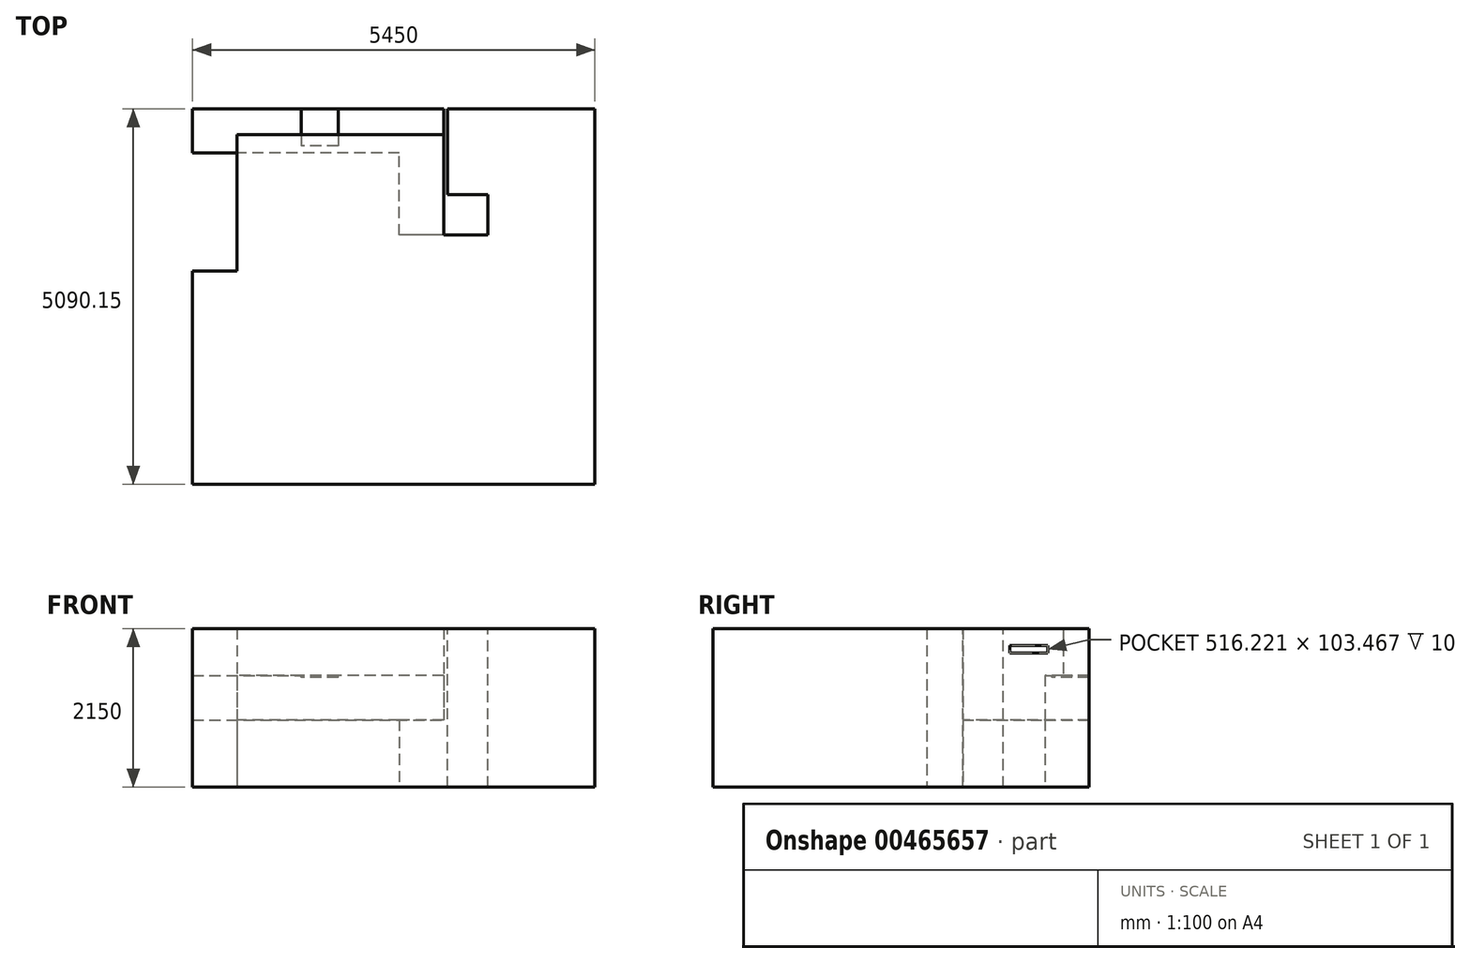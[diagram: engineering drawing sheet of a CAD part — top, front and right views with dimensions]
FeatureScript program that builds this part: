
annotation { "Feature Type Name" : "Feature", "Feature Type Description" : "" }
export const myFeature = defineFeature(function(context is Context, id is Id, definition is map)
    precondition{}
    {
        {
            var Q0;
            Q0=qCreatedBy(makeId("Top.planeOp"),FACE);
            var sketch = newSketch(context, id + "F0", { "sketchPlane" : qUnion([Q0])});
            skLineSegment(sketch, "E0", {"start": v(-1473.18, -1123.99) * mm, "end": v(-1473.18, 1076.01) * mm});
            skLineSegment(sketch, "E1", {"start": v(-1473.18, 1076.01) * mm, "end": v(1926.82, 1076.01) * mm});
            skLineSegment(sketch, "E2", {"start": v(1926.82, 1076.01) * mm, "end": v(1926.82, -633.99) * mm});
            skLineSegment(sketch, "E3", {"start": v(1926.82, -633.99) * mm, "end": v(1326.82, -633.99) * mm});
            skLineSegment(sketch, "E4", {"start": v(1326.82, -633.99) * mm, "end": v(1326.82, 476.01) * mm});
            skLineSegment(sketch, "E5", {"start": v(1326.82, 476.01) * mm, "end": v(-873.18, 476.01) * mm});
            skLineSegment(sketch, "E6", {"start": v(-873.18, 476.01) * mm, "end": v(-873.18, -1123.99) * mm});
            skLineSegment(sketch, "E7", {"start": v(-873.18, -1123.99) * mm, "end": v(-1473.18, -1123.99) * mm});
            skSolve(sketch);
        }
        {
            var Q0;
            Q0=makeQuery(id+"F0.imprint","IMPRINT",FACE,{"disambiguationData":[TD([[makeQuery(id+"F0.imprint","IMPRINT",EDGE,{"derivedFrom":sQuery(id+"F0.wireOp",EDGE,"E0")}),-1.0]])]});
            extrude(context, id + "F1", {"entities" : qUnion([Q0]), "depth" : 910 * mm});
        }
        {
            var Q0;
            Q0=makeQuery(id+"F1.opExtrude","CAP_FACE",FACE,{"disambiguationData":[OSD([sQuery(id+"F0.wireOp",EDGE,"E0"),sQuery(id+"F0.wireOp",EDGE,"E1"),sQuery(id+"F0.wireOp",EDGE,"E2"),sQuery(id+"F0.wireOp",EDGE,"E3"),sQuery(id+"F0.wireOp",EDGE,"E4"),sQuery(id+"F0.wireOp",EDGE,"E5"),sQuery(id+"F0.wireOp",EDGE,"E6"),sQuery(id+"F0.wireOp",EDGE,"E7")])],"isStart":false});
            var sketch = newSketch(context, id + "F2", { "sketchPlane" : qUnion([Q0])});
            skLineSegment(sketch, "E8.bottom", {"start": v(-1473.18, -1123.99) * mm, "end": v(-873.18, -1123.99) * mm});
            skLineSegment(sketch, "E8.top", {"start": v(-1473.18, 476.01) * mm, "end": v(-873.18, 476.01) * mm});
            skLineSegment(sketch, "E8.left", {"start": v(-1473.18, -1123.99) * mm, "end": v(-1473.18, 476.01) * mm});
            skLineSegment(sketch, "E8.right", {"start": v(-873.18, -1123.99) * mm, "end": v(-873.18, 476.01) * mm});
            skSolve(sketch);
        }
        {
            var Q0;
            Q0=makeQuery(id+"F2.imprint","IMPRINT",FACE,{"disambiguationData":[TD([[makeQuery(id+"F2.imprint","IMPRINT",EDGE,{"derivedFrom":sQuery(id+"F2.wireOp",EDGE,"E8.bottom")}),-1.0]])]});
            extrude(context, id + "F3", {"entities" : qUnion([Q0]), "operationType" : NewBodyOperationType.ADD, "depth" : 605 * mm});
        }
        {
            var Q0;
            Q0=makeQuery(id+"F3.opExtrude","CAP_FACE",FACE,{"disambiguationData":[OSD([sQuery(id+"F2.wireOp",EDGE,"E8.bottom"),sQuery(id+"F2.wireOp",EDGE,"E8.top"),sQuery(id+"F2.wireOp",EDGE,"E8.left"),sQuery(id+"F2.wireOp",EDGE,"E8.right")])],"isStart":false});
            var sketch = newSketch(context, id + "F4", { "sketchPlane" : qUnion([Q0])});
            skLineSegment(sketch, "E9", {"start": v(-873.18, -1123.99) * mm, "end": v(-1473.18, -1123.99) * mm});
            skLineSegment(sketch, "E10", {"start": v(-1473.18, -1123.99) * mm, "end": v(-1473.18, 1076.01) * mm});
            skLineSegment(sketch, "E11", {"start": v(-1473.18, 1076.01) * mm, "end": v(1926.82, 1076.01) * mm});
            skLineSegment(sketch, "E12", {"start": v(1926.82, 1076.01) * mm, "end": v(1926.82, 726.01) * mm});
            skLineSegment(sketch, "E13", {"start": v(1926.82, 726.01) * mm, "end": v(-873.18, 726.01) * mm});
            skLineSegment(sketch, "E14", {"start": v(-873.18, 726.01) * mm, "end": v(-873.18, 476.01) * mm});
            skLineSegment(sketch, "E15", {"start": v(-873.18, 476.01) * mm, "end": v(-873.18, 476.01) * mm});
            skLineSegment(sketch, "E16", {"start": v(-873.18, 476.01) * mm, "end": v(-873.18, -1123.99) * mm});
            skSolve(sketch);
        }
        {
            var Q0;
            {var subQ0=sQuery(id+"F4.wireOp",EDGE,"E11");Q0=makeQuery(id+"F4.imprint","IMPRINT",FACE,{"disambiguationData":[TD([[makeQuery(id+"F4.imprint","IMPRINT",EDGE,{"derivedFrom":subQ0}),-1.0]])]});}
            var Q1;
            {var subQ0=sQuery(id+"F4.wireOp",EDGE,"E9");Q1=makeQuery(id+"F4.imprint","IMPRINT",FACE,{"disambiguationData":[TD([[makeQuery(id+"F4.imprint","IMPRINT",EDGE,{"derivedFrom":subQ0}),-1.0]])]});}
            extrude(context, id + "F5", {"entities" : qUnion([Q0, Q1]), "operationType" : NewBodyOperationType.ADD, "depth" : 635 * mm});
        }
        {
            var Q0;
            Q0=makeQuery(id+"F5.opExtrude","CAP_FACE",FACE,{"disambiguationData":[OSD([sQuery(id+"F4.wireOp",EDGE,"E9"),sQuery(id+"F4.wireOp",EDGE,"E10"),sQuery(id+"F4.wireOp",EDGE,"E11"),sQuery(id+"F4.wireOp",EDGE,"E12"),sQuery(id+"F4.wireOp",EDGE,"E13"),sQuery(id+"F4.wireOp",EDGE,"E14"),sQuery(id+"F4.wireOp",EDGE,"E16")])],"isStart":true});
            var sketch = newSketch(context, id + "F6", { "sketchPlane" : qUnion([Q0])});
            skLineSegment(sketch, "E17.left", {"start": v(500, -1076.01) * mm, "end": v(500, -576.01) * mm});
            skLineSegment(sketch, "E17.right", {"start": v(0, -1076.01) * mm, "end": v(0, -576.01) * mm});
            skLineSegment(sketch, "E18", {"start": v(500, -1076.01) * mm, "end": v(0, -1076.01) * mm});
            skLineSegment(sketch, "E19", {"start": v(500, -576.01) * mm, "end": v(0, -576.01) * mm});
            skSolve(sketch);
        }
        {
            var Q0;
            {var subQ0=sQuery(id+"F6.wireOp",EDGE,"E19");Q0=makeQuery(id+"F6.imprint","IMPRINT",FACE,{"disambiguationData":[TD([[makeQuery(id+"F6.imprint","IMPRINT",EDGE,{"derivedFrom":subQ0}),1.0]])]});}
            var Q1;
            {var subQ0=sQuery(id+"F6.wireOp",EDGE,"E18");Q1=makeQuery(id+"F6.imprint","IMPRINT",FACE,{"disambiguationData":[TD([[makeQuery(id+"F6.imprint","IMPRINT",EDGE,{"derivedFrom":subQ0}),1.0]])]});}
            extrude(context, id + "F7", {"entities" : qUnion([Q0, Q1]), "operationType" : NewBodyOperationType.ADD, "depth" : 25 * mm});
        }
        {
            var Q0;
            Q0=makeQuery(id+"F1.opExtrude","CAP_FACE",FACE,{"disambiguationData":[OSD([sQuery(id+"F0.wireOp",EDGE,"E0"),sQuery(id+"F0.wireOp",EDGE,"E1"),sQuery(id+"F0.wireOp",EDGE,"E2"),sQuery(id+"F0.wireOp",EDGE,"E3"),sQuery(id+"F0.wireOp",EDGE,"E4"),sQuery(id+"F0.wireOp",EDGE,"E5"),sQuery(id+"F0.wireOp",EDGE,"E6"),sQuery(id+"F0.wireOp",EDGE,"E7")])],"isStart":true});
            var sketch = newSketch(context, id + "F8", { "sketchPlane" : qUnion([Q0])});
            skLineSegment(sketch, "E20.bottom", {"start": v(1926.82, -1076.01) * mm, "end": v(1976.82, -1076.01) * mm});
            skLineSegment(sketch, "E20.top", {"start": v(1926.82, 633.99) * mm, "end": v(1976.82, 633.99) * mm});
            skLineSegment(sketch, "E20.left", {"start": v(1926.82, -1076.01) * mm, "end": v(1926.82, 633.99) * mm});
            skLineSegment(sketch, "E20.right", {"start": v(1976.82, -1076.01) * mm, "end": v(1976.82, 633.99) * mm});
            skSolve(sketch);
        }
        {
            var Q0;
            Q0=makeQuery(id+"F8.imprint","IMPRINT",FACE,{"disambiguationData":[TD([[makeQuery(id+"F8.imprint","IMPRINT",EDGE,{"derivedFrom":sQuery(id+"F8.wireOp",EDGE,"E20.bottom")}),1.0]])]});
            var Q1;
            Q1=makeQuery(id+"F5.opExtrude","CAP_FACE",FACE,{"disambiguationData":[OSD([sQuery(id+"F4.wireOp",EDGE,"E9"),sQuery(id+"F4.wireOp",EDGE,"E10"),sQuery(id+"F4.wireOp",EDGE,"E11"),sQuery(id+"F4.wireOp",EDGE,"E12"),sQuery(id+"F4.wireOp",EDGE,"E13"),sQuery(id+"F4.wireOp",EDGE,"E14"),sQuery(id+"F4.wireOp",EDGE,"E16")])],"isStart":false});
            extrude(context, id + "F9", {"entities" : qUnion([Q0]), "operationType" : NewBodyOperationType.ADD, "endBound" : BoundingType.UP_TO_SURFACE, "oppositeDirection" : true, "endBoundEntityFace" : qUnion([Q1]), "depth" : 25 * mm});
        }
        {
            var Q0;
            {var subQ0=sQuery(id+"F4.wireOp",EDGE,"E16");var subQ1=sQuery(id+"F4.wireOp",EDGE,"E14");var subQ2=sQuery(id+"F4.wireOp",EDGE,"E13");var subQ3=sQuery(id+"F4.wireOp",EDGE,"E12");var subQ4=sQuery(id+"F4.wireOp",EDGE,"E11");var subQ5=sQuery(id+"F4.wireOp",EDGE,"E10");var subQ6=sQuery(id+"F4.wireOp",EDGE,"E9");Q0=makeQuery(id+"F9.boolean.opBoolean","MERGE",FACE,{"derivedFrom":[makeQuery(id+"F5.opExtrude","CAP_FACE",FACE,{"disambiguationData":[OSD([subQ6,subQ5,subQ4,subQ3,subQ2,subQ1,subQ0])],"isStart":false}),makeQuery(id+"F9.opExtrude","CAP_FACE",FACE,{"disambiguationData":[OSD([subQ6,subQ5,subQ4,subQ3,subQ2,subQ1,subQ0])],"isStart":false})]});}
            var sketch = newSketch(context, id + "F10", { "sketchPlane" : qUnion([Q0])});
            skLineSegment(sketch, "E21.bottom", {"start": v(-1473.18, 1076.01) * mm, "end": v(3976.82, 1076.01) * mm});
            skLineSegment(sketch, "E21.top", {"start": v(-1473.18, 1276.01) * mm, "end": v(3976.82, 1276.01) * mm});
            skLineSegment(sketch, "E21.left", {"start": v(-1473.18, 1076.01) * mm, "end": v(-1473.18, 1276.01) * mm});
            skLineSegment(sketch, "E21.right", {"start": v(3976.82, 1076.01) * mm, "end": v(3976.82, 1276.01) * mm});
            skLineSegment(sketch, "E22.bottom", {"start": v(1976.82, 1076.01) * mm, "end": v(2526.82, 1076.01) * mm});
            skLineSegment(sketch, "E22.top", {"start": v(1976.82, 526.01) * mm, "end": v(2526.82, 526.01) * mm});
            skLineSegment(sketch, "E22.left", {"start": v(1976.82, 1076.01) * mm, "end": v(1976.82, 526.01) * mm});
            skLineSegment(sketch, "E22.right", {"start": v(2526.82, 1076.01) * mm, "end": v(2526.82, 526.01) * mm});
            skLineSegment(sketch, "E23.bottom", {"start": v(1976.82, -633.99) * mm, "end": v(2526.82, -633.99) * mm});
            skLineSegment(sketch, "E23.top", {"start": v(1976.82, -83.99) * mm, "end": v(2526.82, -83.99) * mm});
            skLineSegment(sketch, "E23.left", {"start": v(1976.82, -633.99) * mm, "end": v(1976.82, -83.99) * mm});
            skLineSegment(sketch, "E23.right", {"start": v(2526.82, -633.99) * mm, "end": v(2526.82, -83.99) * mm});
            skLineSegment(sketch, "E24.bottom", {"start": v(3976.82, 1276.01) * mm, "end": v(4246, 1276.01) * mm});
            skLineSegment(sketch, "E24.top", {"start": v(3976.82, -4014.14) * mm, "end": v(4246, -4014.14) * mm});
            skLineSegment(sketch, "E24.left", {"start": v(3976.82, 1276.01) * mm, "end": v(3976.82, -4014.14) * mm});
            skLineSegment(sketch, "E24.right", {"start": v(4246, 1276.01) * mm, "end": v(4246, -4014.14) * mm});
            skLineSegment(sketch, "E25.bottom", {"start": v(4246, -4014.14) * mm, "end": v(-1473.18, -4014.14) * mm});
            skLineSegment(sketch, "E25.top", {"start": v(4246, -4186.1) * mm, "end": v(-1473.18, -4186.1) * mm});
            skLineSegment(sketch, "E25.left", {"start": v(4246, -4014.14) * mm, "end": v(4246, -4186.1) * mm});
            skLineSegment(sketch, "E25.right", {"start": v(-1473.18, -4014.14) * mm, "end": v(-1473.18, -4186.1) * mm});
            skLineSegment(sketch, "E26.bottom", {"start": v(-1473.18, -4186.1) * mm, "end": v(-1635.22, -4186.1) * mm});
            skLineSegment(sketch, "E26.top", {"start": v(-1473.18, 1276.01) * mm, "end": v(-1635.22, 1276.01) * mm});
            skLineSegment(sketch, "E26.left", {"start": v(-1473.18, -4186.1) * mm, "end": v(-1473.18, 1276.01) * mm});
            skLineSegment(sketch, "E26.right", {"start": v(-1635.22, -4186.1) * mm, "end": v(-1635.22, 1276.01) * mm});
            skSolve(sketch);
        }
        {
            var Q0;
            Q0=makeQuery(id+"F10.imprint","IMPRINT",FACE,{"disambiguationData":[TD([[makeQuery(id+"F10.imprint","IMPRINT",EDGE,{"derivedFrom":sQuery(id+"F10.wireOp",EDGE,"E23.bottom")}),1.0]])]});
            var Q1;
            Q1=makeQuery(id+"F10.imprint","IMPRINT",FACE,{"disambiguationData":[TD([[makeQuery(id+"F10.imprint","IMPRINT",EDGE,{"derivedFrom":sQuery(id+"F10.wireOp",EDGE,"E22.bottom")}),-1.0]])]});
            var Q2;
            {var subQ1=sQuery(id+"F10.wireOp",EDGE,"E21.top");Q2=makeQuery(id+"F10.imprint","IMPRINT",FACE,{"disambiguationData":[TD([[makeQuery(id+"F10.imprint","IMPRINT",EDGE,{"derivedFrom":subQ1}),-1.0]])]});}
            var Q3;
            {var subQ5=sQuery(id+"F10.wireOp",EDGE,"E24.bottom");Q3=makeQuery(id+"F10.imprint","IMPRINT",FACE,{"disambiguationData":[TD([[makeQuery(id+"F10.imprint","IMPRINT",EDGE,{"derivedFrom":subQ5}),-1.0]])]});}
            var Q4;
            {var subQ1=sQuery(id+"F10.wireOp",EDGE,"E25.top");Q4=makeQuery(id+"F10.imprint","IMPRINT",FACE,{"disambiguationData":[TD([[makeQuery(id+"F10.imprint","IMPRINT",EDGE,{"derivedFrom":subQ1}),-1.0]])]});}
            var Q5;
            {var subQ3=sQuery(id+"F10.wireOp",EDGE,"E26.bottom");Q5=makeQuery(id+"F10.imprint","IMPRINT",FACE,{"disambiguationData":[TD([[makeQuery(id+"F10.imprint","IMPRINT",EDGE,{"derivedFrom":subQ3}),-1.0]])]});}
            var Q6;
            Q6=makeQuery(id+"F9.boolean.opBoolean","MERGE",FACE,{"derivedFrom":[makeQuery(id+"F1.opExtrude","CAP_FACE",FACE,{"disambiguationData":[OSD([sQuery(id+"F0.wireOp",EDGE,"E0"),sQuery(id+"F0.wireOp",EDGE,"E1"),sQuery(id+"F0.wireOp",EDGE,"E2"),sQuery(id+"F0.wireOp",EDGE,"E3"),sQuery(id+"F0.wireOp",EDGE,"E4"),sQuery(id+"F0.wireOp",EDGE,"E5"),sQuery(id+"F0.wireOp",EDGE,"E6"),sQuery(id+"F0.wireOp",EDGE,"E7")])],"isStart":true}),makeQuery(id+"F9.opExtrude","CAP_FACE",FACE,{"disambiguationData":[OSD([sQuery(id+"F8.wireOp",EDGE,"E20.bottom"),sQuery(id+"F8.wireOp",EDGE,"E20.top"),sQuery(id+"F8.wireOp",EDGE,"E20.left"),sQuery(id+"F8.wireOp",EDGE,"E20.right")])],"isStart":true})]});
            extrude(context, id + "F11", {"entities" : qUnion([Q0, Q1, Q2, Q3, Q4, Q5]), "operationType" : NewBodyOperationType.ADD, "endBound" : BoundingType.UP_TO_SURFACE, "oppositeDirection" : true, "endBoundEntityFace" : qUnion([Q6]), "depth" : 25 * mm});
        }
        {
            var Q0;
            Q0=makeQuery(id+"F11.opExtrude","SWEPT_FACE",FACE,{"disambiguationData":[OSD([sQuery(id+"F10.wireOp",EDGE,"E24.left")])]});
            var sketch = newSketch(context, id + "F12", { "sketchPlane" : qUnion([Q0])});
            skLineSegment(sketch, "E27.bottom", {"start": v(0, 1815.75) * mm, "end": v(-516.22, 1815.75) * mm});
            skLineSegment(sketch, "E27.top", {"start": v(0, 1919.21) * mm, "end": v(-516.22, 1919.21) * mm});
            skLineSegment(sketch, "E27.left", {"start": v(0, 1815.75) * mm, "end": v(0, 1919.21) * mm});
            skLineSegment(sketch, "E27.right", {"start": v(-516.22, 1815.75) * mm, "end": v(-516.22, 1919.21) * mm});
            skSolve(sketch);
        }
        {
            var Q0;
            Q0 = qSketchRegion(id + "F12", true);
            extrude(context, id + "F13", {"entities" : qUnion([Q0]), "operationType" : NewBodyOperationType.ADD, "depth" : 10 * mm});
        }
        {
            var Q0;
            {var subQ0=sQuery(id+"F4.wireOp",EDGE,"E16");var subQ1=sQuery(id+"F4.wireOp",EDGE,"E14");var subQ2=sQuery(id+"F4.wireOp",EDGE,"E13");var subQ3=sQuery(id+"F4.wireOp",EDGE,"E12");var subQ4=sQuery(id+"F4.wireOp",EDGE,"E11");var subQ5=sQuery(id+"F4.wireOp",EDGE,"E10");var subQ6=sQuery(id+"F4.wireOp",EDGE,"E9");Q0=makeQuery(id+"F11.boolean.opBoolean","MERGE",FACE,{"derivedFrom":[makeQuery(id+"F9.boolean.opBoolean","MERGE",FACE,{"derivedFrom":[makeQuery(id+"F5.opExtrude","CAP_FACE",FACE,{"disambiguationData":[OSD([subQ6,subQ5,subQ4,subQ3,subQ2,subQ1,subQ0])],"isStart":false}),makeQuery(id+"F9.opExtrude","CAP_FACE",FACE,{"disambiguationData":[OSD([subQ6,subQ5,subQ4,subQ3,subQ2,subQ1,subQ0])],"isStart":false})]}),makeQuery(id+"F11.opExtrude","CAP_FACE",FACE,{"disambiguationData":[OSD([sQuery(id+"F10.wireOp",EDGE,"E21.bottom"),sQuery(id+"F10.wireOp",EDGE,"E21.top"),sQuery(id+"F10.wireOp",EDGE,"E22.top"),sQuery(id+"F10.wireOp",EDGE,"E22.left"),sQuery(id+"F10.wireOp",EDGE,"E22.right"),sQuery(id+"F10.wireOp",EDGE,"E24.bottom"),sQuery(id+"F10.wireOp",EDGE,"E24.left"),sQuery(id+"F10.wireOp",EDGE,"E24.right"),sQuery(id+"F10.wireOp",EDGE,"E25.bottom"),sQuery(id+"F10.wireOp",EDGE,"E25.top"),sQuery(id+"F10.wireOp",EDGE,"E25.left"),sQuery(id+"F10.wireOp",EDGE,"E26.bottom"),sQuery(id+"F10.wireOp",EDGE,"E26.top"),sQuery(id+"F10.wireOp",EDGE,"E26.left"),sQuery(id+"F10.wireOp",EDGE,"E26.right")])],"isStart":true}),makeQuery(id+"F11.opExtrude","CAP_FACE",FACE,{"disambiguationData":[OSD([sQuery(id+"F10.wireOp",EDGE,"E23.bottom"),sQuery(id+"F10.wireOp",EDGE,"E23.top"),sQuery(id+"F10.wireOp",EDGE,"E23.left"),sQuery(id+"F10.wireOp",EDGE,"E23.right")])],"isStart":true})]});}
            var sketch = newSketch(context, id + "F14", { "sketchPlane" : qUnion([Q0])});
            skLineSegment(sketch, "E28.bottom", {"start": v(-1635.22, -4186.1) * mm, "end": v(4246, -4186.1) * mm});
            skLineSegment(sketch, "E28.top", {"start": v(-1635.22, 1276.01) * mm, "end": v(4246, 1276.01) * mm});
            skLineSegment(sketch, "E28.left", {"start": v(-1635.22, -4186.1) * mm, "end": v(-1635.22, 1276.01) * mm});
            skLineSegment(sketch, "E28.right", {"start": v(4246, -4186.1) * mm, "end": v(4246, 1276.01) * mm});
            skSolve(sketch);
        }
        {
            var Q0;
            Q0 = qSketchRegion(id + "F14", true);
            var Q1;
            {var subQ0=sQuery(id+"F8.wireOp",EDGE,"E20.right");var subQ1=sQuery(id+"F8.wireOp",EDGE,"E20.left");var subQ2=sQuery(id+"F8.wireOp",EDGE,"E20.top");var subQ3=sQuery(id+"F8.wireOp",EDGE,"E20.bottom");var subQ4=sQuery(id+"F0.wireOp",EDGE,"E7");var subQ5=sQuery(id+"F0.wireOp",EDGE,"E6");var subQ6=sQuery(id+"F0.wireOp",EDGE,"E5");var subQ7=sQuery(id+"F0.wireOp",EDGE,"E4");var subQ8=sQuery(id+"F0.wireOp",EDGE,"E3");var subQ9=sQuery(id+"F0.wireOp",EDGE,"E2");var subQ10=sQuery(id+"F0.wireOp",EDGE,"E1");var subQ11=sQuery(id+"F0.wireOp",EDGE,"E0");var subQ12=sQuery(id+"F10.wireOp",EDGE,"E21.bottom");Q1=makeQuery(id+"F11.boolean.opBoolean","MERGE",FACE,{"derivedFrom":[makeQuery(id+"F9.boolean.opBoolean","MERGE",FACE,{"derivedFrom":[makeQuery(id+"F1.opExtrude","CAP_FACE",FACE,{"disambiguationData":[OSD([subQ11,subQ10,subQ9,subQ8,subQ7,subQ6,subQ5,subQ4])],"isStart":true}),makeQuery(id+"F9.opExtrude","CAP_FACE",FACE,{"disambiguationData":[OSD([subQ3,subQ2,subQ1,subQ0])],"isStart":true})]}),makeQuery(id+"F11.opExtrude","CAP_FACE",FACE,{"disambiguationData":[OSD([subQ11,subQ10,subQ9,subQ8,subQ7,subQ6,subQ5,subQ4,subQ3,subQ2,subQ1,subQ0]),ownerDisambiguation([makeQuery(id+"F10.imprint","IMPRINT",EDGE,{"disambiguationData":[TD([[makeQuery(id+"F10.imprint","INTERSECT",VERTEX,{"derivedFrom":[subQ12,sQuery(id+"F10.wireOp",EDGE,"E26.left")]}),-1.0]])],"derivedFrom":subQ12})])],"isStart":false}),makeQuery(id+"F11.opExtrude","CAP_FACE",FACE,{"disambiguationData":[OSD([subQ11,subQ10,subQ9,subQ8,subQ7,subQ6,subQ5,subQ4,subQ3,subQ2,subQ1,subQ0]),ownerDisambiguation([makeQuery(id+"F10.imprint","IMPRINT",EDGE,{"derivedFrom":sQuery(id+"F10.wireOp",EDGE,"E23.bottom")})])],"isStart":false})]});}
            extrude(context, id + "F15", {"entities" : qUnion([Q0]), "endBound" : BoundingType.UP_TO_SURFACE, "oppositeDirection" : true, "endBoundEntityFace" : qUnion([Q1]), "depth" : 25 * mm});
        }
        {
            var Q0;
            Q0=makeQuery(id+"F1.opExtrude","SWEPT_BODY",BODY,{"disambiguationData":[OSD([sQuery(id+"F0.wireOp",EDGE,"E0"),sQuery(id+"F0.wireOp",EDGE,"E1"),sQuery(id+"F0.wireOp",EDGE,"E2"),sQuery(id+"F0.wireOp",EDGE,"E3"),sQuery(id+"F0.wireOp",EDGE,"E4"),sQuery(id+"F0.wireOp",EDGE,"E5"),sQuery(id+"F0.wireOp",EDGE,"E6"),sQuery(id+"F0.wireOp",EDGE,"E7")])]});
            var Q1;
            Q1=makeQuery(id+"F15.opExtrude","SWEPT_BODY",BODY,{"disambiguationData":[OSD([sQuery(id+"F14.wireOp",EDGE,"E28.bottom"),sQuery(id+"F14.wireOp",EDGE,"E28.top"),sQuery(id+"F14.wireOp",EDGE,"E28.left"),sQuery(id+"F14.wireOp",EDGE,"E28.right")])]});
            booleanBodies(context, id + "F16", {"operationType" : BooleanOperationType.SUBTRACTION, "tools" : qUnion([Q0]), "targets" : qUnion([Q1])});
        }
    });
